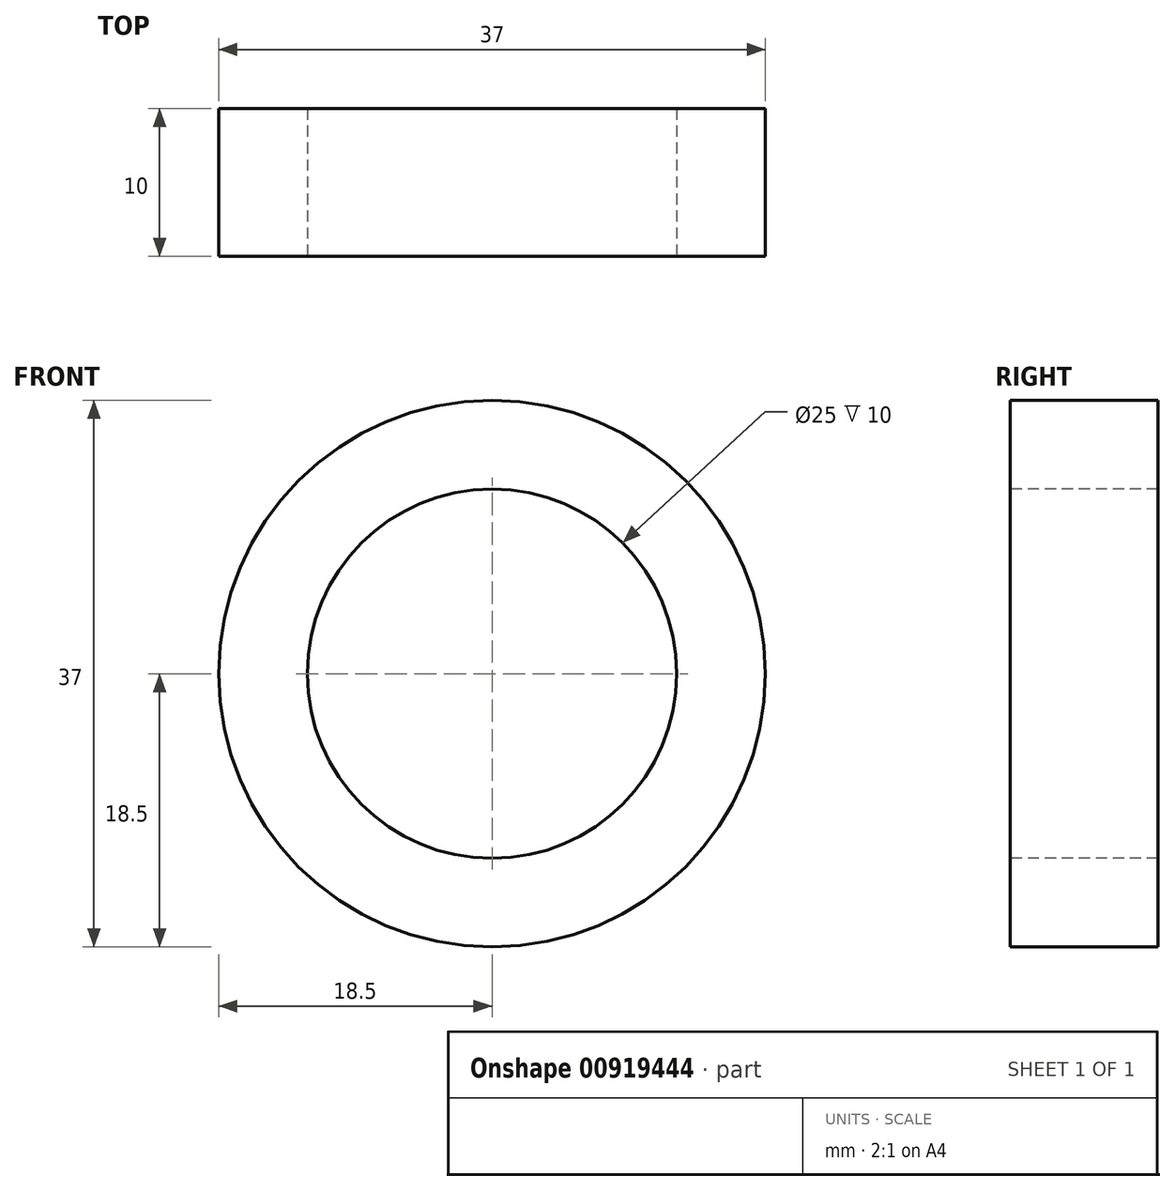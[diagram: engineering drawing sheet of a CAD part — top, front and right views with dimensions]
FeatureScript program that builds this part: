
annotation { "Feature Type Name" : "Feature", "Feature Type Description" : "" }
export const myFeature = defineFeature(function(context is Context, id is Id, definition is map)
    precondition{}
    {
        {
            var Q0;
            Q0=qCreatedBy(makeId("Right.planeOp"),FACE);
            var sketch = newSketch(context, id + "F0", { "sketchPlane" : qUnion([Q0])});
            skLineSegment(sketch, "E0", {"start": v(0, 16.73) * mm, "end": v(0, -61.73) * mm, "construction": true});
            skLineSegment(sketch, "E1.bottom", {"start": v(-5, -18.5) * mm, "end": v(5, -18.5) * mm});
            skLineSegment(sketch, "E1.top", {"start": v(-5, -12.5) * mm, "end": v(5, -12.5) * mm});
            skLineSegment(sketch, "E1.left", {"start": v(-5, -18.5) * mm, "end": v(-5, -12.5) * mm});
            skLineSegment(sketch, "E1.right", {"start": v(5, -18.5) * mm, "end": v(5, -12.5) * mm});
            skPoint(sketch, "E1.middle", {"position": v(0, -15.5) * mm});
            skLineSegment(sketch, "E2", {"start": v(-23.88, 0) * mm, "end": v(34.09, 0) * mm, "construction": true});
            skSolve(sketch);
        }
        {
            var Q0;
            Q0=makeQuery(id+"F0.imprint","IMPRINT",FACE,{"disambiguationData":[TD([[makeQuery(id+"F0.imprint","IMPRINT",EDGE,{"derivedFrom":sQuery(id+"F0.wireOp",EDGE,"E1.bottom")}),1.0]])]});
            var Q1;
            Q1=sQuery(id+"F0.wireOp",EDGE,"E2");
            revolve(context, id + "F1", {"surfaceOperationType" : NewSurfaceOperationType.NEW, "entities" : qUnion([Q0]), "axis" : qUnion([Q1]), "revolveType" : RevolveType.FULL});
        }
    });
